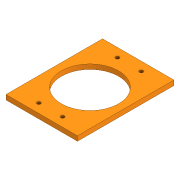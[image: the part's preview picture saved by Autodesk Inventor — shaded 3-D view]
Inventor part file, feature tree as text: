
AUTODESK INVENTOR PART (.ipt)
format: ipt  version: 2020.3 (Build 243373000, 373)  size: 103,936 bytes
history: native  units: mm
features: extrude x1, sketch x1
ambient origin geometry x8: Origin, YZ Plane, XZ Plane, XY Plane, X Axis, Y Axis, Z Axis, Center Point
bodies: Solid1 (feature_tree)
feature tree (2):
  extrude  "Extrusion1"  Depth=4.0mm
  sketch  "Sketch1"  dims[d1=81.0mm d6=7.5mm d7=5.0mm d8=30.0mm d9=3.0mm d10=7.5mm d11=5.0mm d12=3.0mm d13=3.0mm d14=5.0mm d15=48.0mm d16=4.0mm d17=0.0mm]
